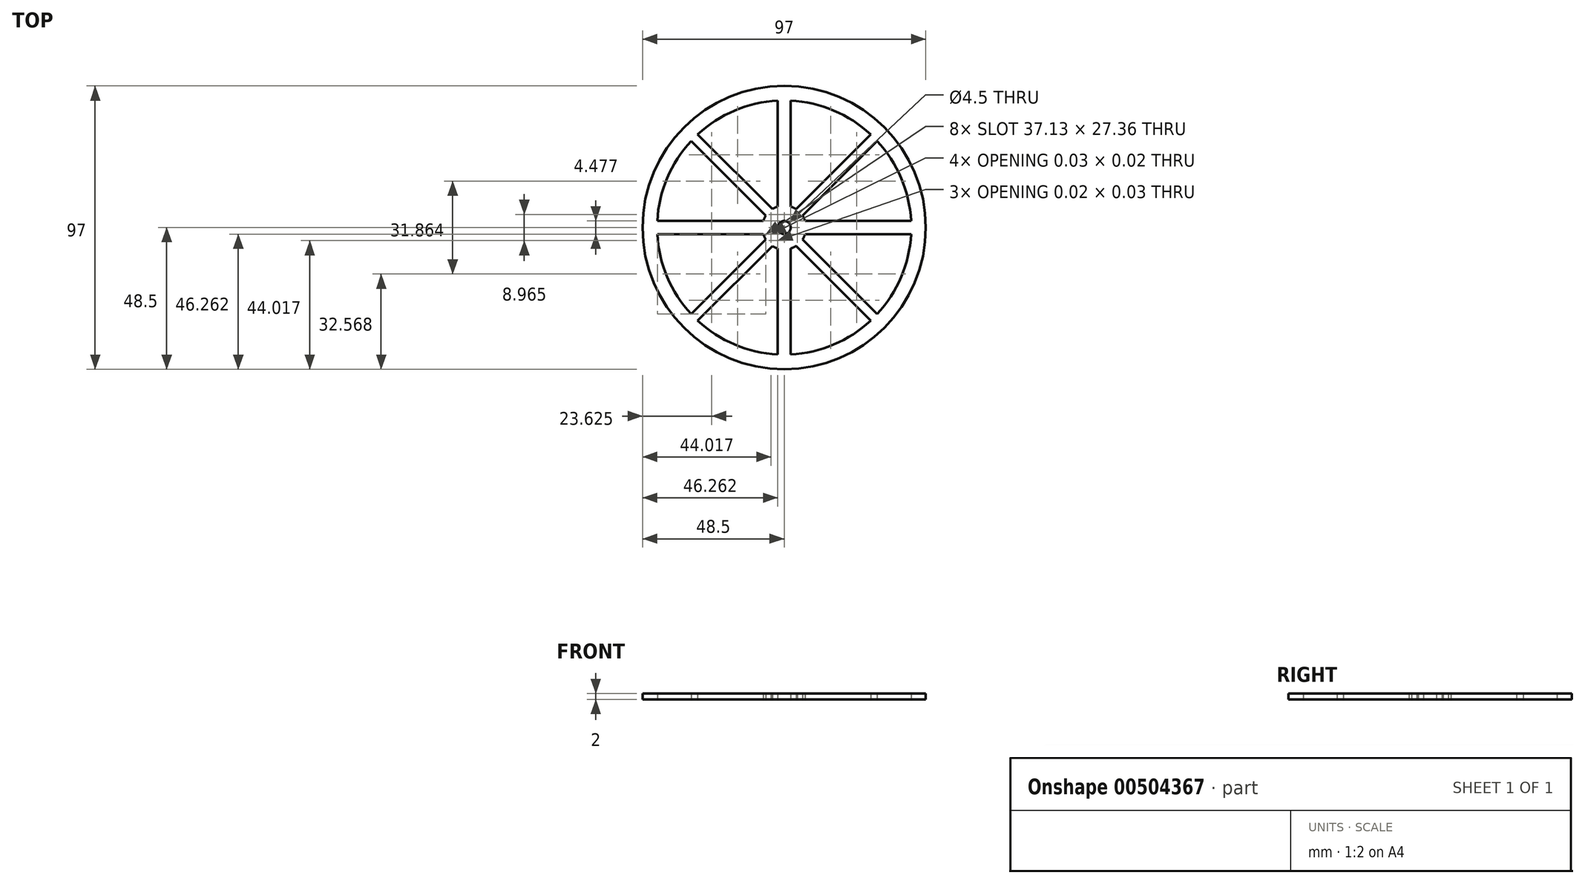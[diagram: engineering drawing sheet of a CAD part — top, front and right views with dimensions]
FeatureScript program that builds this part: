
annotation { "Feature Type Name" : "Feature", "Feature Type Description" : "" }
export const myFeature = defineFeature(function(context is Context, id is Id, definition is map)
    precondition{}
    {
        {
            var Q0;
            Q0=qCreatedBy(makeId("Top.planeOp"),FACE);
            var sketch = newSketch(context, id + "F0", { "sketchPlane" : qUnion([Q0])});
            skCircle(sketch, "E0", {"center": v(0, 0) * mm, "radius": 48.5 * mm});
            skArc(sketch, "E1", {"start": v(-43.44, -2.25) * mm, "mid": v(-40.06, -16.95) * mm, "end": v(-31.86, -29.61) * mm});
            skCircle(sketch, "E2", {"center": v(0, 0) * mm, "radius": 2.25 * mm});
            skLineSegment(sketch, "E3", {"start": v(2.25, 4.47) * mm, "end": v(2.25, 4.5) * mm});
            skLineSegment(sketch, "E4", {"start": v(-4.47, 2.25) * mm, "end": v(-4.5, 2.25) * mm});
            skLineSegment(sketch, "E5", {"start": v(0, 0) * mm, "end": v(-30.76, 30.76) * mm, "construction": true});
            skLineSegment(sketch, "E6", {"start": v(-4.48, 2.23) * mm, "end": v(-4.5, 2.25) * mm});
            skLineSegment(sketch, "E7", {"start": v(-2.23, 4.48) * mm, "end": v(-2.25, 4.5) * mm});
            skLineSegment(sketch, "E8.MirrorCS", {"start": v(2.25, -7.15) * mm, "end": v(2.25, -43.44) * mm});
            skLineSegment(sketch, "E9.MirrorCS", {"start": v(-2.23, -4.48) * mm, "end": v(-2.25, -4.5) * mm});
            skLineSegment(sketch, "E10.MirrorCS", {"start": v(-4.48, -2.23) * mm, "end": v(-4.5, -2.25) * mm});
            skLineSegment(sketch, "E11.MirrorCS", {"start": v(2.23, 4.48) * mm, "end": v(2.25, 4.5) * mm});
            skLineSegment(sketch, "E12.MirrorCS", {"start": v(4.48, 2.23) * mm, "end": v(4.5, 2.25) * mm});
            skLineSegment(sketch, "E13.MirrorCS", {"start": v(2.23, -4.48) * mm, "end": v(2.25, -4.5) * mm});
            skLineSegment(sketch, "E14.MirrorCS", {"start": v(4.48, -2.23) * mm, "end": v(4.5, -2.25) * mm});
            skArc(sketch, "E15", {"start": v(-4.47, 2.25) * mm, "mid": v(-4.47, 2.24) * mm, "end": v(-4.48, 2.23) * mm});
            skPoint(sketch, "E16.orphan", {"position": v(0, 2.25) * mm});
            skPoint(sketch, "E17.orphan", {"position": v(-2.25, 0) * mm});
            skPoint(sketch, "E18.orphan", {"position": v(0, -2.25) * mm});
            skPoint(sketch, "E19.orphan", {"position": v(2.25, 0) * mm});
            skLineSegment(sketch, "E20.trimOffspring", {"start": v(4.47, -2.25) * mm, "end": v(4.5, -2.25) * mm});
            skLineSegment(sketch, "E21.trimOffspring", {"start": v(-2.25, -4.47) * mm, "end": v(-2.25, -4.5) * mm});
            skLineSegment(sketch, "E22.trimOffspring", {"start": v(-4.47, -2.25) * mm, "end": v(-4.5, -2.25) * mm});
            skLineSegment(sketch, "E23.trimOffspring", {"start": v(4.47, 2.25) * mm, "end": v(4.5, 2.25) * mm});
            skLineSegment(sketch, "E24.trimOffspring", {"start": v(-2.25, 4.47) * mm, "end": v(-2.25, 4.5) * mm});
            skArc(sketch, "E25.trimOffspring", {"start": v(-4.48, -2.23) * mm, "mid": v(-4.47, -2.24) * mm, "end": v(-4.47, -2.25) * mm});
            skArc(sketch, "E26.trimOffspring", {"start": v(-2.25, -4.47) * mm, "mid": v(-2.24, -4.47) * mm, "end": v(-2.23, -4.48) * mm});
            skArc(sketch, "E27.trimOffspring", {"start": v(4.47, -2.25) * mm, "mid": v(4.47, -2.24) * mm, "end": v(4.48, -2.23) * mm});
            skArc(sketch, "E28.trimOffspring", {"start": v(2.25, 4.47) * mm, "mid": v(2.24, 4.47) * mm, "end": v(2.23, 4.48) * mm});
            skArc(sketch, "E29.trimOffspring", {"start": v(-2.23, 4.48) * mm, "mid": v(-2.24, 4.47) * mm, "end": v(-2.25, 4.47) * mm});
            skArc(sketch, "E30.trimOffspring", {"start": v(4.48, 2.23) * mm, "mid": v(4.47, 2.24) * mm, "end": v(4.47, 2.25) * mm});
            skArc(sketch, "E31", {"start": v(-6.3, 4.06) * mm, "mid": v(-6.8, 3.18) * mm, "end": v(-7.15, 2.25) * mm});
            skLineSegment(sketch, "E32.trimOffspring", {"start": v(-2.25, 7.15) * mm, "end": v(-2.25, 43.44) * mm});
            skLineSegment(sketch, "E33.trimOffspring", {"start": v(-4.06, 6.3) * mm, "end": v(-29.61, 31.86) * mm});
            skLineSegment(sketch, "E34.trimOffspring", {"start": v(-6.3, 4.06) * mm, "end": v(-31.86, 29.61) * mm});
            skLineSegment(sketch, "E35.trimOffspring", {"start": v(-7.15, 2.25) * mm, "end": v(-43.44, 2.25) * mm});
            skLineSegment(sketch, "E36.trimOffspring", {"start": v(-6.3, -4.06) * mm, "end": v(-31.86, -29.61) * mm});
            skLineSegment(sketch, "E37.trimOffspring", {"start": v(-7.15, -2.25) * mm, "end": v(-43.44, -2.25) * mm});
            skArc(sketch, "E38.trimOffspring", {"start": v(-7.15, -2.25) * mm, "mid": v(-6.8, -3.18) * mm, "end": v(-6.3, -4.06) * mm});
            skArc(sketch, "E39.trimOffspring", {"start": v(-4.06, -6.3) * mm, "mid": v(-3.18, -6.8) * mm, "end": v(-2.25, -7.15) * mm});
            skLineSegment(sketch, "E40.trimOffspring", {"start": v(-2.25, -7.15) * mm, "end": v(-2.25, -43.44) * mm});
            skLineSegment(sketch, "E41.trimOffspring", {"start": v(-4.06, -6.3) * mm, "end": v(-29.61, -31.86) * mm});
            skArc(sketch, "E42.trimOffspring", {"start": v(2.25, -7.15) * mm, "mid": v(3.18, -6.8) * mm, "end": v(4.06, -6.3) * mm});
            skLineSegment(sketch, "E43.trimOffspring", {"start": v(4.06, -6.3) * mm, "end": v(29.61, -31.86) * mm});
            skArc(sketch, "E44.trimOffspring", {"start": v(6.3, -4.06) * mm, "mid": v(7.05, 2.55) * mm, "end": v(2.25, 7.15) * mm});
            skLineSegment(sketch, "E45.trimOffspring", {"start": v(7.15, -2.25) * mm, "end": v(43.44, -2.25) * mm});
            skLineSegment(sketch, "E46.trimOffspring", {"start": v(6.3, -4.06) * mm, "end": v(31.86, -29.61) * mm});
            skLineSegment(sketch, "E47.trimOffspring", {"start": v(7.15, 2.25) * mm, "end": v(43.44, 2.25) * mm});
            skLineSegment(sketch, "E48.trimOffspring", {"start": v(6.3, 4.06) * mm, "end": v(31.86, 29.61) * mm});
            skLineSegment(sketch, "E49.trimOffspring", {"start": v(4.06, 6.3) * mm, "end": v(29.61, 31.86) * mm});
            skLineSegment(sketch, "E50.trimOffspring", {"start": v(2.25, 7.15) * mm, "end": v(2.25, 43.44) * mm});
            skArc(sketch, "E51.trimOffspring", {"start": v(-2.25, 7.15) * mm, "mid": v(-3.18, 6.8) * mm, "end": v(-4.06, 6.3) * mm});
            skArc(sketch, "E52.trimOffspring", {"start": v(-29.61, -31.86) * mm, "mid": v(-16.95, -40.06) * mm, "end": v(-2.25, -43.44) * mm});
            skArc(sketch, "E53.trimOffspring", {"start": v(2.25, -43.44) * mm, "mid": v(16.95, -40.06) * mm, "end": v(29.61, -31.86) * mm});
            skArc(sketch, "E54.trimOffspring", {"start": v(31.86, -29.61) * mm, "mid": v(40.06, -16.95) * mm, "end": v(43.44, -2.25) * mm});
            skArc(sketch, "E55.trimOffspring", {"start": v(43.44, 2.25) * mm, "mid": v(40.06, 16.95) * mm, "end": v(31.86, 29.61) * mm});
            skArc(sketch, "E56.trimOffspring", {"start": v(29.61, 31.86) * mm, "mid": v(16.95, 40.06) * mm, "end": v(2.25, 43.44) * mm});
            skArc(sketch, "E57.trimOffspring", {"start": v(-2.25, 43.44) * mm, "mid": v(-16.95, 40.06) * mm, "end": v(-29.61, 31.86) * mm});
            skArc(sketch, "E58.trimOffspring", {"start": v(-31.86, 29.61) * mm, "mid": v(-40.06, 16.95) * mm, "end": v(-43.44, 2.25) * mm});
            skSolve(sketch);
        }
        {
            var Q0;
            Q0 = qSketchRegion(id + "F0", true);
            extrude(context, id + "F1", {"entities" : qUnion([Q0]), "depth" : 2 * mm});
        }
    });
